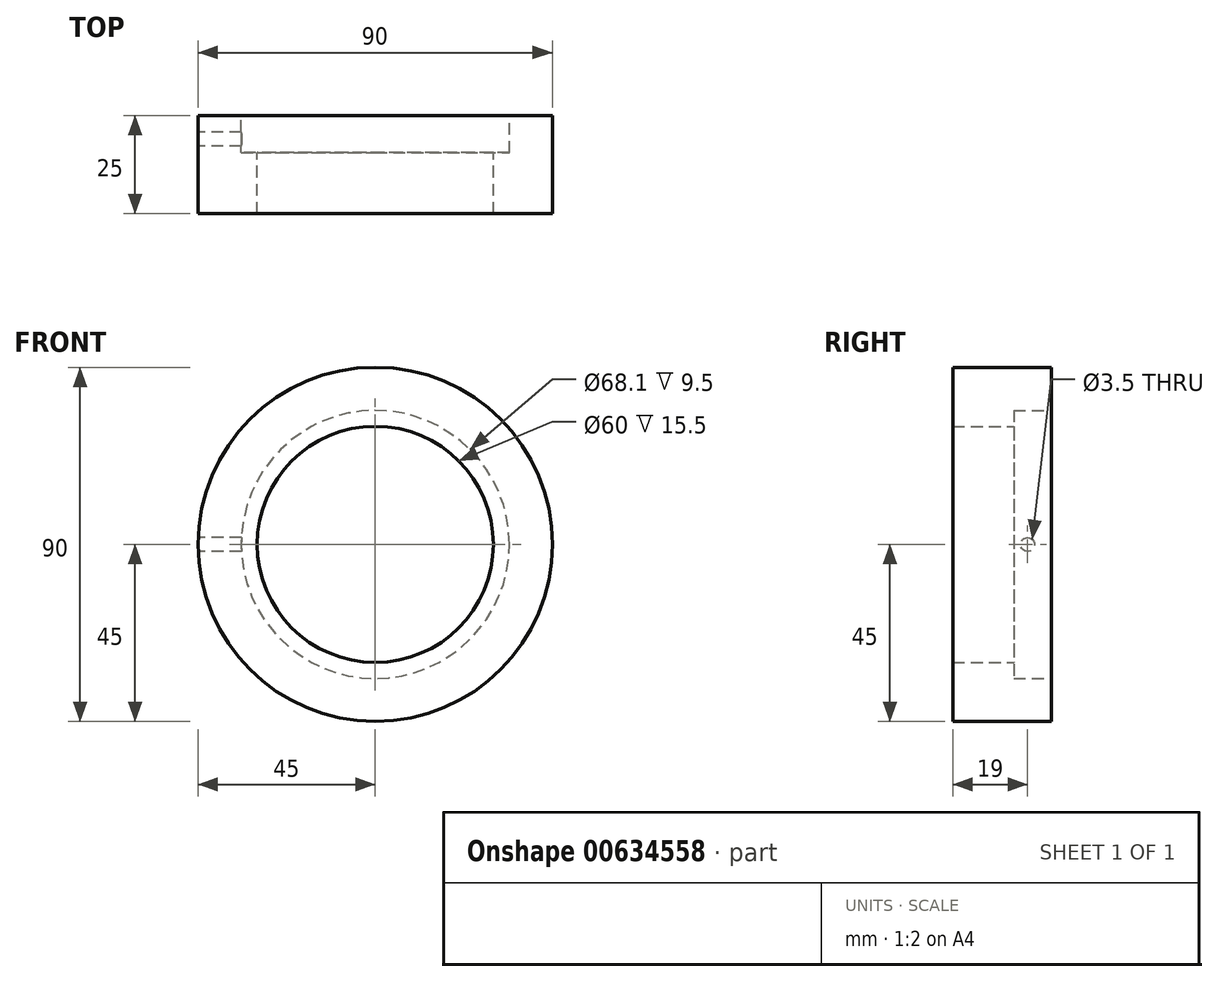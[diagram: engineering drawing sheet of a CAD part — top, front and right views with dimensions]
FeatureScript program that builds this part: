
annotation { "Feature Type Name" : "Feature", "Feature Type Description" : "" }
export const myFeature = defineFeature(function(context is Context, id is Id, definition is map)
    precondition{}
    {
        {
            var Q0;
            Q0=qCreatedBy(makeId("Front.planeOp"),FACE);
            var sketch = newSketch(context, id + "F0", { "sketchPlane" : qUnion([Q0])});
            skCircle(sketch, "E0", {"center": v(0, 0) * mm, "radius": 30 * mm});
            skCircle(sketch, "E1", {"center": v(0, 0) * mm, "radius": 45 * mm});
            skSolve(sketch);
        }
        {
            var Q0;
            Q0 = qSketchRegion(id + "F0", true);
            extrude(context, id + "F1", {"entities" : qUnion([Q0]), "depth" : 25 * mm, "offsetDistance" : 25 * mm});
        }
        {
            var Q0;
            Q0=makeQuery(id+"F1.opExtrude","CAP_FACE",FACE,{"disambiguationData":[OSD([sQuery(id+"F0.wireOp",EDGE,"E0"),sQuery(id+"F0.wireOp",EDGE,"E1")])],"isStart":true});
            var sketch = newSketch(context, id + "F2", { "sketchPlane" : qUnion([Q0])});
            skCircle(sketch, "E2", {"center": v(0, 0) * mm, "radius": 34.05 * mm});
            skSolve(sketch);
        }
        {
            var Q0;
            Q0 = qSketchRegion(id + "F2", true);
            extrude(context, id + "F3", {"entities" : qUnion([Q0]), "operationType" : NewBodyOperationType.REMOVE, "oppositeDirection" : true, "depth" : 9.5 * mm, "offsetDistance" : 25 * mm});
        }
        {
            var Q0;
            Q0=qCreatedBy(makeId("Right.planeOp"),FACE);
            cPlane(context, id + "F4", {"entities" : qUnion([Q0]), "cplaneType" : CPlaneType.OFFSET, "offset" : 45 * mm, "oppositeDirection" : true, "width" : 150 * mm, "height" : 150 * mm});
        }
        {
            var Q0;
            Q0=qCreatedBy(id+"F4.planeOp",FACE);
            var sketch = newSketch(context, id + "F5", { "sketchPlane" : qUnion([Q0])});
            skCircle(sketch, "E3", {"center": v(-6, 0) * mm, "radius": 1.75 * mm});
            skSolve(sketch);
        }
        {
            var Q0;
            Q0 = qSketchRegion(id + "F5", true);
            extrude(context, id + "F6", {"entities" : qUnion([Q0]), "operationType" : NewBodyOperationType.REMOVE, "depth" : 25 * mm, "offsetDistance" : 25 * mm});
        }
    });
